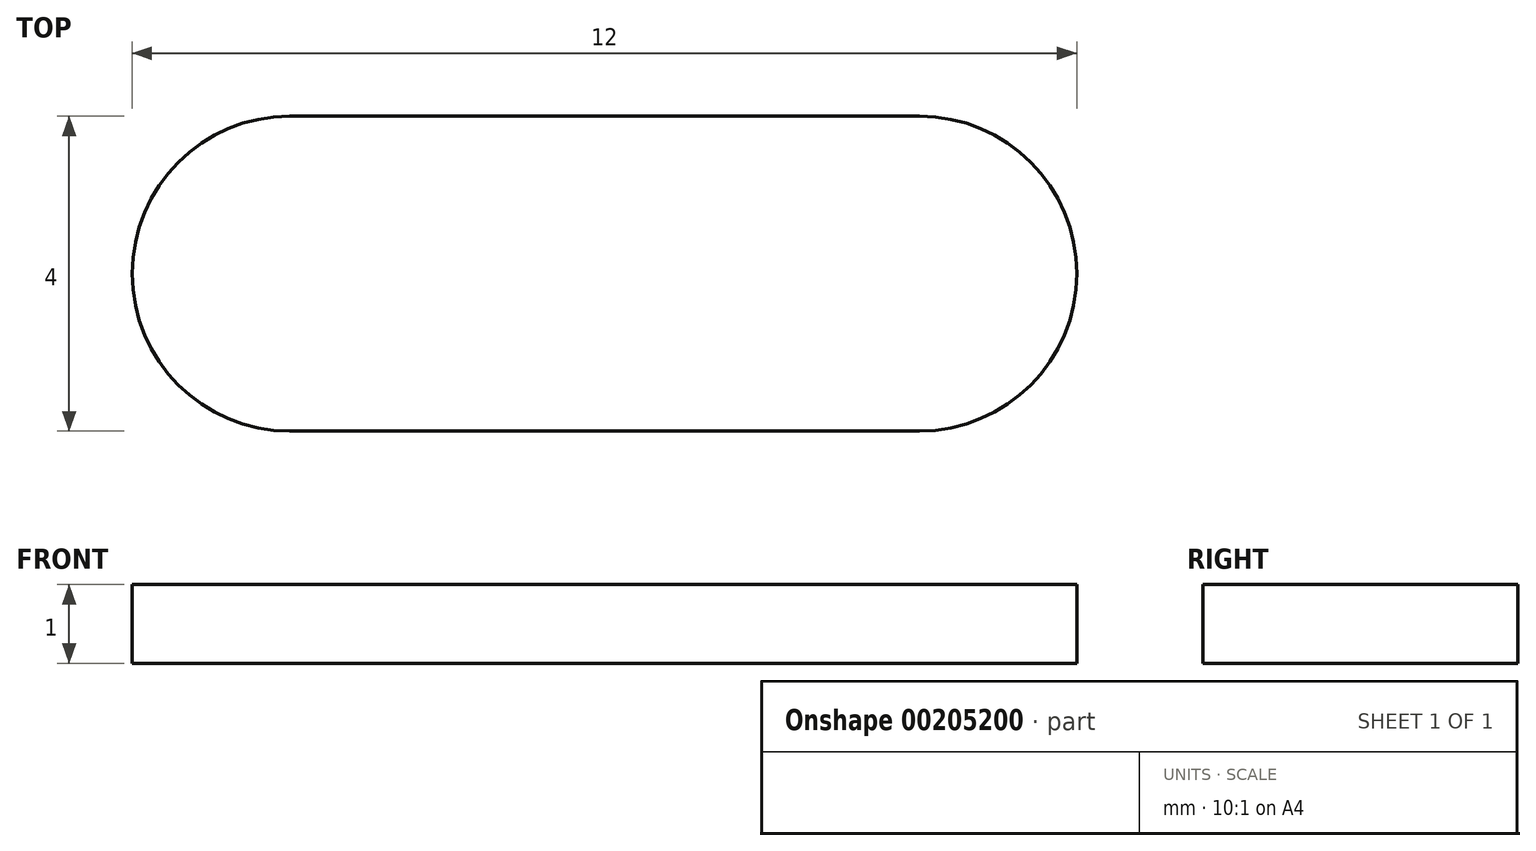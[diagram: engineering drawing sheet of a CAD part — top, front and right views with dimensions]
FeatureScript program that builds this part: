
annotation { "Feature Type Name" : "Feature", "Feature Type Description" : "" }
export const myFeature = defineFeature(function(context is Context, id is Id, definition is map)
    precondition{}
    {
        {
            var Q0;
            Q0=qCreatedBy(makeId("Top.planeOp"),FACE);
            var sketch = newSketch(context, id + "F0", { "sketchPlane" : qUnion([Q0])});
            skLineSegment(sketch, "E0.bottom", {"start": v(-4, 2) * mm, "end": v(4, 2) * mm});
            skLineSegment(sketch, "E0.top", {"start": v(-4, -2) * mm, "end": v(4, -2) * mm});
            skLineSegment(sketch, "E0.left", {"start": v(-6, 0) * mm, "end": v(-6, 0) * mm});
            skLineSegment(sketch, "E0.right", {"start": v(6, 0) * mm, "end": v(6, 0) * mm});
            skPoint(sketch, "E0.middle", {"position": v(0, 0) * mm});
            skPoint(sketch, "E1.visualSharp", {"position": v(6, 2) * mm});
            skArc(sketch, "E1.filletArc", {"start": v(6, 0) * mm, "mid": v(5.41, 1.41) * mm, "end": v(4, 2) * mm});
            skPoint(sketch, "E2.visualSharp", {"position": v(6, -2) * mm});
            skArc(sketch, "E2.filletArc", {"start": v(4, -2) * mm, "mid": v(5.41, -1.41) * mm, "end": v(6, 0) * mm});
            skPoint(sketch, "E3.visualSharp", {"position": v(-6, -2) * mm});
            skArc(sketch, "E3.filletArc", {"start": v(-6, 0) * mm, "mid": v(-5.41, -1.41) * mm, "end": v(-4, -2) * mm});
            skPoint(sketch, "E4.visualSharp", {"position": v(-6, 2) * mm});
            skArc(sketch, "E4.filletArc", {"start": v(-4, 2) * mm, "mid": v(-5.41, 1.41) * mm, "end": v(-6, 0) * mm});
            skSolve(sketch);
        }
        {
            var Q0;
            Q0 = qSketchRegion(id + "F0", true);
            extrude(context, id + "F1", {"entities" : qUnion([Q0]), "depth" : 1 * mm});
        }
    });
